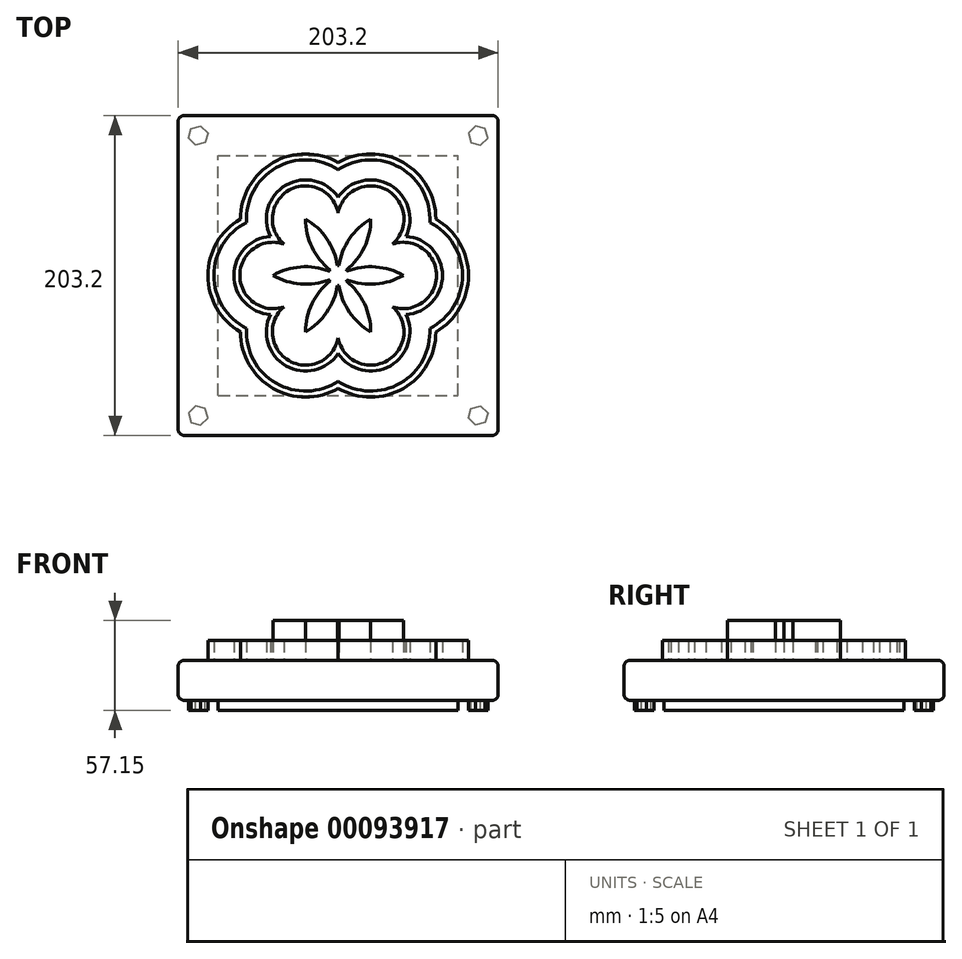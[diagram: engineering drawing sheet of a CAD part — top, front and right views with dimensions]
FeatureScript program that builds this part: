
annotation { "Feature Type Name" : "Feature", "Feature Type Description" : "" }
export const myFeature = defineFeature(function(context is Context, id is Id, definition is map)
    precondition{}
    {
        {
            var Q0;
            Q0=qCreatedBy(makeId("Top.planeOp"),FACE);
            var sketch = newSketch(context, id + "F0", { "sketchPlane" : qUnion([Q0])});
            skLineSegment(sketch, "E0.bottom", {"start": v(-101.6, 101.6) * mm, "end": v(101.6, 101.6) * mm});
            skLineSegment(sketch, "E0.top", {"start": v(-101.6, -101.6) * mm, "end": v(101.6, -101.6) * mm});
            skLineSegment(sketch, "E0.left", {"start": v(-101.6, 101.6) * mm, "end": v(-101.6, -101.6) * mm});
            skLineSegment(sketch, "E0.right", {"start": v(101.6, 101.6) * mm, "end": v(101.6, -101.6) * mm});
            skPoint(sketch, "E0.middle", {"position": v(0, 0) * mm});
            skSolve(sketch);
        }
        {
            var Q0;
            Q0=makeQuery(id+"F0.imprint","IMPRINT",FACE,{"disambiguationData":[TD([[makeQuery(id+"F0.imprint","IMPRINT",EDGE,{"derivedFrom":sQuery(id+"F0.wireOp",EDGE,"E0.bottom")}),-1.0]])]});
            extrude(context, id + "F1", {"entities" : qUnion([Q0]), "depth" : 25.4 * mm});
        }
        {
            var Q0;
            Q0=makeQuery(id+"F1.opExtrude","CAP_FACE",FACE,{"disambiguationData":[OSD([sQuery(id+"F0.wireOp",EDGE,"E0.bottom"),sQuery(id+"F0.wireOp",EDGE,"E0.top"),sQuery(id+"F0.wireOp",EDGE,"E0.left"),sQuery(id+"F0.wireOp",EDGE,"E0.right")])],"isStart":true});
            var sketch = newSketch(context, id + "F2", { "sketchPlane" : qUnion([Q0])});
            skPoint(sketch, "E1.middle", {"position": v(0, 0) * mm});
            skLineSegment(sketch, "E2.0", {"start": v(-76.2, 76.2) * mm, "end": v(76.2, 76.2) * mm});
            skLineSegment(sketch, "E2.1", {"start": v(-76.2, 76.2) * mm, "end": v(-76.2, -76.2) * mm});
            skLineSegment(sketch, "E2.2", {"start": v(-76.2, -76.2) * mm, "end": v(76.2, -76.2) * mm});
            skLineSegment(sketch, "E2.3", {"start": v(76.2, 76.2) * mm, "end": v(76.2, -76.2) * mm});
            skLineSegment(sketch, "E3.bottom", {"start": v(-76.2, 76.2) * mm, "end": v(-101.6, 76.2) * mm, "construction": true});
            skLineSegment(sketch, "E3.top", {"start": v(-76.2, 101.6) * mm, "end": v(-101.6, 101.6) * mm, "construction": true});
            skLineSegment(sketch, "E3.left", {"start": v(-76.2, 76.2) * mm, "end": v(-76.2, 101.6) * mm, "construction": true});
            skLineSegment(sketch, "E3.right", {"start": v(-101.6, 76.2) * mm, "end": v(-101.6, 101.6) * mm, "construction": true});
            skLineSegment(sketch, "E4.bottom", {"start": v(76.2, 76.2) * mm, "end": v(101.6, 76.2) * mm, "construction": true});
            skLineSegment(sketch, "E4.top", {"start": v(76.2, 101.6) * mm, "end": v(101.6, 101.6) * mm, "construction": true});
            skLineSegment(sketch, "E4.left", {"start": v(76.2, 76.2) * mm, "end": v(76.2, 101.6) * mm, "construction": true});
            skLineSegment(sketch, "E4.right", {"start": v(101.6, 76.2) * mm, "end": v(101.6, 101.6) * mm, "construction": true});
            skLineSegment(sketch, "E5.bottom", {"start": v(76.2, -76.2) * mm, "end": v(101.6, -76.2) * mm, "construction": true});
            skLineSegment(sketch, "E5.top", {"start": v(76.2, -101.6) * mm, "end": v(101.6, -101.6) * mm, "construction": true});
            skLineSegment(sketch, "E5.left", {"start": v(76.2, -76.2) * mm, "end": v(76.2, -101.6) * mm, "construction": true});
            skLineSegment(sketch, "E5.right", {"start": v(101.6, -76.2) * mm, "end": v(101.6, -101.6) * mm, "construction": true});
            skLineSegment(sketch, "E6.bottom", {"start": v(-76.2, -76.2) * mm, "end": v(-101.6, -76.2) * mm, "construction": true});
            skLineSegment(sketch, "E6.top", {"start": v(-76.2, -101.6) * mm, "end": v(-101.6, -101.6) * mm, "construction": true});
            skLineSegment(sketch, "E6.left", {"start": v(-76.2, -76.2) * mm, "end": v(-76.2, -101.6) * mm, "construction": true});
            skLineSegment(sketch, "E6.right", {"start": v(-101.6, -76.2) * mm, "end": v(-101.6, -101.6) * mm, "construction": true});
            skLineSegment(sketch, "E7", {"start": v(-101.6, 76.2) * mm, "end": v(-76.2, 101.6) * mm, "construction": true});
            skCircle(sketch, "E8.cCircle", {"center": v(-88.9, 88.9) * mm, "radius": 5.5 * mm, "construction": true});
            skLineSegment(sketch, "E8.0", {"start": v(-90.54, 82.77) * mm, "end": v(-95.03, 87.26) * mm});
            skLineSegment(sketch, "E8.1", {"start": v(-95.03, 87.26) * mm, "end": v(-93.4, 93.4) * mm});
            skLineSegment(sketch, "E8.2", {"start": v(-93.4, 93.4) * mm, "end": v(-87.26, 95.03) * mm});
            skLineSegment(sketch, "E8.3", {"start": v(-87.26, 95.03) * mm, "end": v(-82.77, 90.54) * mm});
            skLineSegment(sketch, "E8.4", {"start": v(-82.77, 90.54) * mm, "end": v(-84.4, 84.4) * mm});
            skLineSegment(sketch, "E8.5", {"start": v(-84.4, 84.4) * mm, "end": v(-90.54, 82.77) * mm});
            skPoint(sketch, "E8.0.midPoint", {"position": v(-92.79, 85.01) * mm});
            skLineSegment(sketch, "E9", {"start": v(0, 101.6) * mm, "end": v(0, -101.6) * mm, "construction": true});
            skLineSegment(sketch, "E10", {"start": v(-101.6, 0) * mm, "end": v(101.6, 0) * mm, "construction": true});
            skLineSegment(sketch, "E11.MirrorCS", {"start": v(-90.54, -82.77) * mm, "end": v(-95.03, -87.26) * mm});
            skLineSegment(sketch, "E12.MirrorCS", {"start": v(-95.03, -87.26) * mm, "end": v(-93.4, -93.4) * mm});
            skLineSegment(sketch, "E13.MirrorCS", {"start": v(-93.4, -93.4) * mm, "end": v(-87.26, -95.03) * mm});
            skLineSegment(sketch, "E14.MirrorCS", {"start": v(-87.26, -95.03) * mm, "end": v(-82.77, -90.54) * mm});
            skLineSegment(sketch, "E15.MirrorCS", {"start": v(-82.77, -90.54) * mm, "end": v(-84.4, -84.4) * mm});
            skLineSegment(sketch, "E16.MirrorCS", {"start": v(-84.4, -84.4) * mm, "end": v(-90.54, -82.77) * mm});
            skLineSegment(sketch, "E17.MirrorCS", {"start": v(87.26, 95.03) * mm, "end": v(82.77, 90.54) * mm});
            skLineSegment(sketch, "E18.MirrorCS", {"start": v(82.77, 90.54) * mm, "end": v(84.4, 84.4) * mm});
            skLineSegment(sketch, "E19.MirrorCS", {"start": v(93.4, 93.4) * mm, "end": v(87.26, 95.03) * mm});
            skLineSegment(sketch, "E20.MirrorCS", {"start": v(95.03, 87.26) * mm, "end": v(93.4, 93.4) * mm});
            skLineSegment(sketch, "E21.MirrorCS", {"start": v(90.54, 82.77) * mm, "end": v(95.03, 87.26) * mm});
            skLineSegment(sketch, "E22.MirrorCS", {"start": v(84.4, 84.4) * mm, "end": v(90.54, 82.77) * mm});
            skLineSegment(sketch, "E23.MirrorCS", {"start": v(84.4, -84.4) * mm, "end": v(90.54, -82.77) * mm});
            skLineSegment(sketch, "E24.MirrorCS", {"start": v(90.54, -82.77) * mm, "end": v(95.03, -87.26) * mm});
            skLineSegment(sketch, "E25.MirrorCS", {"start": v(95.03, -87.26) * mm, "end": v(93.4, -93.4) * mm});
            skLineSegment(sketch, "E26.MirrorCS", {"start": v(93.4, -93.4) * mm, "end": v(87.26, -95.03) * mm});
            skLineSegment(sketch, "E27.MirrorCS", {"start": v(87.26, -95.03) * mm, "end": v(82.77, -90.54) * mm});
            skLineSegment(sketch, "E28.MirrorCS", {"start": v(82.77, -90.54) * mm, "end": v(84.4, -84.4) * mm});
            skSolve(sketch);
        }
        {
            var Q0;
            Q0=makeQuery(id+"F2.imprint","IMPRINT",FACE,{"disambiguationData":[TD([[makeQuery(id+"F2.imprint","IMPRINT",EDGE,{"derivedFrom":sQuery(id+"F2.wireOp",EDGE,"E11.MirrorCS")}),1.0]])]});
            var Q1;
            Q1=makeQuery(id+"F2.imprint","IMPRINT",FACE,{"disambiguationData":[TD([[makeQuery(id+"F2.imprint","IMPRINT",EDGE,{"derivedFrom":sQuery(id+"F2.wireOp",EDGE,"E24.MirrorCS")}),-1.0]])]});
            var Q2;
            Q2=makeQuery(id+"F2.imprint","IMPRINT",FACE,{"disambiguationData":[TD([[makeQuery(id+"F2.imprint","IMPRINT",EDGE,{"derivedFrom":sQuery(id+"F2.wireOp",EDGE,"E17.MirrorCS")}),1.0]])]});
            var Q3;
            Q3=makeQuery(id+"F2.imprint","IMPRINT",FACE,{"disambiguationData":[TD([[makeQuery(id+"F2.imprint","IMPRINT",EDGE,{"derivedFrom":sQuery(id+"F2.wireOp",EDGE,"E8.0")}),-1.0]])]});
            extrude(context, id + "F3", {"entities" : qUnion([Q0, Q1, Q2, Q3]), "operationType" : NewBodyOperationType.ADD, "depth" : 6.35 * mm});
        }
        {
            var Q0;
            Q0=makeQuery(id+"F2.imprint","IMPRINT",FACE,{"disambiguationData":[TD([[makeQuery(id+"F2.imprint","IMPRINT",EDGE,{"derivedFrom":sQuery(id+"F2.wireOp",EDGE,"E2.0")}),-1.0]])]});
            extrude(context, id + "F4", {"entities" : qUnion([Q0]), "operationType" : NewBodyOperationType.ADD, "depth" : 6.35 * mm});
        }
        {
            var Q0;
            Q0=makeQuery(id+"F1.opExtrude","CAP_FACE",FACE,{"disambiguationData":[OSD([sQuery(id+"F0.wireOp",EDGE,"E0.bottom"),sQuery(id+"F0.wireOp",EDGE,"E0.top"),sQuery(id+"F0.wireOp",EDGE,"E0.left"),sQuery(id+"F0.wireOp",EDGE,"E0.right")])],"isStart":false});
            var sketch = newSketch(context, id + "F5", { "sketchPlane" : qUnion([Q0])});
            skArc(sketch, "E29", {"start": v(-20.7, -35.84) * mm, "mid": v(-7.24, -23.38) * mm, "end": v(-0.49, -6.33) * mm});
            skArc(sketch, "E30", {"start": v(62.08, -35.84) * mm, "mid": v(82.78, 0) * mm, "end": v(62.08, 35.84) * mm});
            skArc(sketch, "E31", {"start": v(-41.39, 0) * mm, "mid": v(-23.87, -5.42) * mm, "end": v(-5.73, -2.74) * mm});
            skArc(sketch, "E32", {"start": v(62.08, 35.84) * mm, "mid": v(41.39, 71.69) * mm, "end": v(0, 71.69) * mm});
            skArc(sketch, "E33", {"start": v(-62.08, -35.84) * mm, "mid": v(-41.39, -71.69) * mm, "end": v(0, -71.69) * mm});
            skArc(sketch, "E34", {"start": v(0, -71.69) * mm, "mid": v(41.39, -71.69) * mm, "end": v(62.08, -35.84) * mm});
            skArc(sketch, "E35.trimOffspring", {"start": v(20.7, -35.84) * mm, "mid": v(16.63, -17.96) * mm, "end": v(5.24, -3.59) * mm});
            skArc(sketch, "E36.trimOffspring", {"start": v(41.39, 0) * mm, "mid": v(23.87, 5.42) * mm, "end": v(5.73, 2.74) * mm});
            skArc(sketch, "E37.trimOffspring", {"start": v(20.7, 35.84) * mm, "mid": v(7.24, 23.38) * mm, "end": v(0.49, 6.33) * mm});
            skArc(sketch, "E38.trimOffspring", {"start": v(0, 71.69) * mm, "mid": v(-41.39, 71.69) * mm, "end": v(-62.08, 35.84) * mm});
            skArc(sketch, "E39.trimOffspring", {"start": v(-20.7, 35.84) * mm, "mid": v(-16.63, 17.96) * mm, "end": v(-5.24, 3.59) * mm});
            skArc(sketch, "E40.trimOffspring", {"start": v(-62.08, 35.84) * mm, "mid": v(-82.78, 0) * mm, "end": v(-62.08, -35.84) * mm});
            skArc(sketch, "E41.0", {"start": v(58.2, 33.6) * mm, "mid": v(39.48, 68.39) * mm, "end": v(0, 67.2) * mm});
            skArc(sketch, "E41.1", {"start": v(-58.2, 33.6) * mm, "mid": v(-78.97, 0) * mm, "end": v(-58.2, -33.6) * mm});
            skArc(sketch, "E41.2", {"start": v(-58.2, -33.6) * mm, "mid": v(-39.48, -68.39) * mm, "end": v(0, -67.2) * mm});
            skArc(sketch, "E41.3", {"start": v(0, 67.2) * mm, "mid": v(-39.48, 68.39) * mm, "end": v(-58.2, 33.6) * mm});
            skArc(sketch, "E41.4", {"start": v(0, -67.2) * mm, "mid": v(39.48, -68.39) * mm, "end": v(58.2, -33.6) * mm});
            skArc(sketch, "E41.5", {"start": v(58.2, -33.6) * mm, "mid": v(78.97, 0) * mm, "end": v(58.2, 33.6) * mm});
            skArc(sketch, "E42.0", {"start": v(43, 24.83) * mm, "mid": v(33.13, 57.39) * mm, "end": v(0, 49.65) * mm});
            skArc(sketch, "E42.1", {"start": v(-43, 24.83) * mm, "mid": v(-66.27, 0) * mm, "end": v(-43, -24.83) * mm});
            skArc(sketch, "E42.2", {"start": v(-43, -24.83) * mm, "mid": v(-33.13, -57.39) * mm, "end": v(0, -49.65) * mm});
            skArc(sketch, "E42.3", {"start": v(0, 49.65) * mm, "mid": v(-33.13, 57.39) * mm, "end": v(-43, 24.83) * mm});
            skArc(sketch, "E42.4", {"start": v(0, -49.65) * mm, "mid": v(33.13, -57.39) * mm, "end": v(43, -24.83) * mm});
            skArc(sketch, "E42.5", {"start": v(43, -24.83) * mm, "mid": v(66.27, 0) * mm, "end": v(43, 24.83) * mm});
            skArc(sketch, "E43.0", {"start": v(0, 39.8) * mm, "mid": v(-31.23, 54.09) * mm, "end": v(-34.46, 19.9) * mm});
            skArc(sketch, "E43.1", {"start": v(-34.46, -19.9) * mm, "mid": v(-31.23, -54.09) * mm, "end": v(0, -39.8) * mm});
            skArc(sketch, "E43.2", {"start": v(0, -39.8) * mm, "mid": v(31.23, -54.09) * mm, "end": v(34.46, -19.9) * mm});
            skArc(sketch, "E43.3", {"start": v(-34.46, 19.9) * mm, "mid": v(-62.46, 0) * mm, "end": v(-34.46, -19.9) * mm});
            skArc(sketch, "E43.4", {"start": v(34.46, -19.9) * mm, "mid": v(62.46, 0) * mm, "end": v(34.46, 19.9) * mm});
            skArc(sketch, "E43.5", {"start": v(34.46, 19.9) * mm, "mid": v(31.23, 54.09) * mm, "end": v(0, 39.8) * mm});
            skArc(sketch, "E44", {"start": v(-5.24, 3.59) * mm, "mid": v(-5.5, 3.18) * mm, "end": v(-5.73, 2.74) * mm});
            skArc(sketch, "E45.trimOffspring", {"start": v(5.24, 3.59) * mm, "mid": v(16.63, 17.96) * mm, "end": v(20.7, 35.84) * mm});
            skArc(sketch, "E46.trimOffspring", {"start": v(0.49, -6.33) * mm, "mid": v(7.24, -23.38) * mm, "end": v(20.7, -35.84) * mm});
            skArc(sketch, "E47.trimOffspring", {"start": v(-5.24, -3.59) * mm, "mid": v(-16.63, -17.96) * mm, "end": v(-20.7, -35.84) * mm});
            skArc(sketch, "E48.trimOffspring", {"start": v(-0.49, 6.33) * mm, "mid": v(-7.24, 23.38) * mm, "end": v(-20.7, 35.84) * mm});
            skArc(sketch, "E49.trimOffspring", {"start": v(5.73, -2.74) * mm, "mid": v(23.87, -5.42) * mm, "end": v(41.39, 0) * mm});
            skArc(sketch, "E50.trimOffspring", {"start": v(-5.73, 2.74) * mm, "mid": v(-23.87, 5.42) * mm, "end": v(-41.39, 0) * mm});
            skArc(sketch, "E51.trimOffspring", {"start": v(0.49, 6.33) * mm, "mid": v(0, 6.35) * mm, "end": v(-0.49, 6.33) * mm});
            skArc(sketch, "E52.trimOffspring", {"start": v(-5.73, -2.74) * mm, "mid": v(-5.5, -3.18) * mm, "end": v(-5.24, -3.59) * mm});
            skArc(sketch, "E53.trimOffspring", {"start": v(-0.49, -6.33) * mm, "mid": v(0, -6.35) * mm, "end": v(0.49, -6.33) * mm});
            skArc(sketch, "E54.trimOffspring", {"start": v(5.24, -3.59) * mm, "mid": v(5.5, -3.17) * mm, "end": v(5.73, -2.74) * mm});
            skArc(sketch, "E55.trimOffspring", {"start": v(5.73, 2.74) * mm, "mid": v(5.5, 3.17) * mm, "end": v(5.24, 3.59) * mm});
            skSolve(sketch);
        }
        {
            var Q0;
            Q0 = qSketchRegion(id + "F5", true);
            extrude(context, id + "F6", {"entities" : qUnion([Q0]), "operationType" : NewBodyOperationType.ADD, "depth" : 12.7 * mm});
        }
        {
            var Q0;
            Q0=makeQuery(id+"F5.imprint","IMPRINT",FACE,{"disambiguationData":[TD([[makeQuery(id+"F5.imprint","IMPRINT",EDGE,{"derivedFrom":sQuery(id+"F5.wireOp",EDGE,"E42.0")}),1.0]])]});
            extrude(context, id + "F7", {"entities" : qUnion([Q0]), "operationType" : NewBodyOperationType.ADD, "depth" : 12.7 * mm});
        }
        {
            var Q0;
            {var subQ0=sQuery(id+"F5.wireOp",EDGE,"E37.trimOffspring");var subQ1=sQuery(id+"F5.wireOp",EDGE,"E35.trimOffspring");var subQ2=makeQuery(id+"F5.imprint","INTERSECT",VERTEX,{"derivedFrom":[subQ1,subQ0]});Q0=makeQuery(id+"F5.imprint","IMPRINT",FACE,{"disambiguationData":[TD([[makeQuery(id+"F5.imprint","IMPRINT",EDGE,{"disambiguationData":[TD([[subQ2,-1.0]])],"derivedFrom":subQ1}),1.0]])]});}
            extrude(context, id + "F8", {"entities" : qUnion([Q0]), "operationType" : NewBodyOperationType.ADD, "depth" : 12.7 * mm});
        }
        {
            var Q0;
            {var subQ0=sQuery(id+"F5.wireOp",EDGE,"E39.trimOffspring");var subQ1=sQuery(id+"F5.wireOp",EDGE,"E29");var subQ2=makeQuery(id+"F5.imprint","INTERSECT",VERTEX,{"derivedFrom":[subQ1,subQ0]});Q0=makeQuery(id+"F5.imprint","IMPRINT",FACE,{"disambiguationData":[TD([[makeQuery(id+"F5.imprint","IMPRINT",EDGE,{"disambiguationData":[TD([[subQ2,1.0]])],"derivedFrom":subQ1}),1.0]])]});}
            var Q1;
            {var subQ0=sQuery(id+"F5.wireOp",EDGE,"E31");Q1=makeQuery(id+"F5.imprint","IMPRINT",FACE,{"disambiguationData":[TD([[makeQuery(id+"F5.imprint","IMPRINT",EDGE,{"derivedFrom":subQ0}),1.0]])]});}
            var Q2;
            {var subQ0=sQuery(id+"F5.wireOp",EDGE,"E39.trimOffspring");Q2=makeQuery(id+"F5.imprint","IMPRINT",FACE,{"disambiguationData":[TD([[makeQuery(id+"F5.imprint","IMPRINT",EDGE,{"derivedFrom":subQ0}),1.0]])]});}
            var Q3;
            {var subQ0=sQuery(id+"F5.wireOp",EDGE,"E37.trimOffspring");Q3=makeQuery(id+"F5.imprint","IMPRINT",FACE,{"disambiguationData":[TD([[makeQuery(id+"F5.imprint","IMPRINT",EDGE,{"derivedFrom":subQ0}),1.0]])]});}
            var Q4;
            {var subQ0=sQuery(id+"F5.wireOp",EDGE,"E36.trimOffspring");Q4=makeQuery(id+"F5.imprint","IMPRINT",FACE,{"disambiguationData":[TD([[makeQuery(id+"F5.imprint","IMPRINT",EDGE,{"derivedFrom":subQ0}),1.0]])]});}
            var Q5;
            Q5=makeQuery(id+"F8.opExtrude","CAP_FACE",FACE,{"disambiguationData":[OSD([sQuery(id+"F5.wireOp",EDGE,"E35.trimOffspring"),sQuery(id+"F5.wireOp",EDGE,"E44"),sQuery(id+"F5.wireOp",EDGE,"E46.trimOffspring")])],"isStart":false});
            var Q6;
            {var subQ0=sQuery(id+"F5.wireOp",EDGE,"E44");var subQ3=makeQuery(id+"F5.imprint","INTERSECT",VERTEX,{"derivedFrom":[sQuery(id+"F5.wireOp",EDGE,"E36.trimOffspring"),subQ0]});Q6=makeQuery(id+"F5.imprint","IMPRINT",FACE,{"disambiguationData":[TD([[makeQuery(id+"F5.imprint","IMPRINT",EDGE,{"disambiguationData":[TD([[subQ3,-1.0]])],"derivedFrom":subQ0}),1.0]])]});}
            extrude(context, id + "F9", {"entities" : qUnion([Q0, Q1, Q2, Q3, Q4, Q5, Q6]), "operationType" : NewBodyOperationType.ADD, "depth" : 12.7 * mm});
        }
        {
            var Q0;
            Q0=makeQuery(id+"F1.opExtrude","CAP_EDGE",EDGE,{"disambiguationData":[OSD([sQuery(id+"F0.wireOp",EDGE,"E0.bottom")])],"isStart":false});
            var Q1;
            Q1=makeQuery(id+"F1.opExtrude","CAP_EDGE",EDGE,{"disambiguationData":[OSD([sQuery(id+"F0.wireOp",EDGE,"E0.left")])],"isStart":false});
            var Q2;
            Q2=makeQuery(id+"F1.opExtrude","CAP_EDGE",EDGE,{"disambiguationData":[OSD([sQuery(id+"F0.wireOp",EDGE,"E0.right")])],"isStart":false});
            var Q3;
            Q3=makeQuery(id+"F1.opExtrude","CAP_EDGE",EDGE,{"disambiguationData":[OSD([sQuery(id+"F0.wireOp",EDGE,"E0.top")])],"isStart":false});
            var Q4;
            Q4=makeQuery(id+"F1.opExtrude","SWEPT_EDGE",EDGE,{"disambiguationData":[OSD([sQuery(id+"F0.wireOp",EDGE,"E0.bottom"),sQuery(id+"F0.wireOp",EDGE,"E0.right")])]});
            var Q5;
            Q5=makeQuery(id+"F1.opExtrude","SWEPT_EDGE",EDGE,{"disambiguationData":[OSD([sQuery(id+"F0.wireOp",EDGE,"E0.bottom"),sQuery(id+"F0.wireOp",EDGE,"E0.left")])]});
            var Q6;
            Q6=makeQuery(id+"F1.opExtrude","SWEPT_EDGE",EDGE,{"disambiguationData":[OSD([sQuery(id+"F0.wireOp",EDGE,"E0.top"),sQuery(id+"F0.wireOp",EDGE,"E0.left")])]});
            var Q7;
            Q7=makeQuery(id+"F1.opExtrude","SWEPT_EDGE",EDGE,{"disambiguationData":[OSD([sQuery(id+"F0.wireOp",EDGE,"E0.top"),sQuery(id+"F0.wireOp",EDGE,"E0.right")])]});
            var Q8;
            Q8=makeQuery(id+"F1.opExtrude","CAP_EDGE",EDGE,{"disambiguationData":[OSD([sQuery(id+"F0.wireOp",EDGE,"E0.right")])],"isStart":true});
            var Q9;
            Q9=makeQuery(id+"F1.opExtrude","CAP_EDGE",EDGE,{"disambiguationData":[OSD([sQuery(id+"F0.wireOp",EDGE,"E0.top")])],"isStart":true});
            var Q10;
            Q10=makeQuery(id+"F1.opExtrude","CAP_EDGE",EDGE,{"disambiguationData":[OSD([sQuery(id+"F0.wireOp",EDGE,"E0.left")])],"isStart":true});
            var Q11;
            Q11=makeQuery(id+"F1.opExtrude","CAP_EDGE",EDGE,{"disambiguationData":[OSD([sQuery(id+"F0.wireOp",EDGE,"E0.bottom")])],"isStart":true});
            fillet(context, id + "F10", {"entities" : qUnion([Q0, Q1, Q2, Q3, Q4, Q5, Q6, Q7, Q8, Q9, Q10, Q11]), "radius" : 3.8 * mm, "tangentPropagation" : true, "allowEdgeOverflow" : false});
        }
    });
